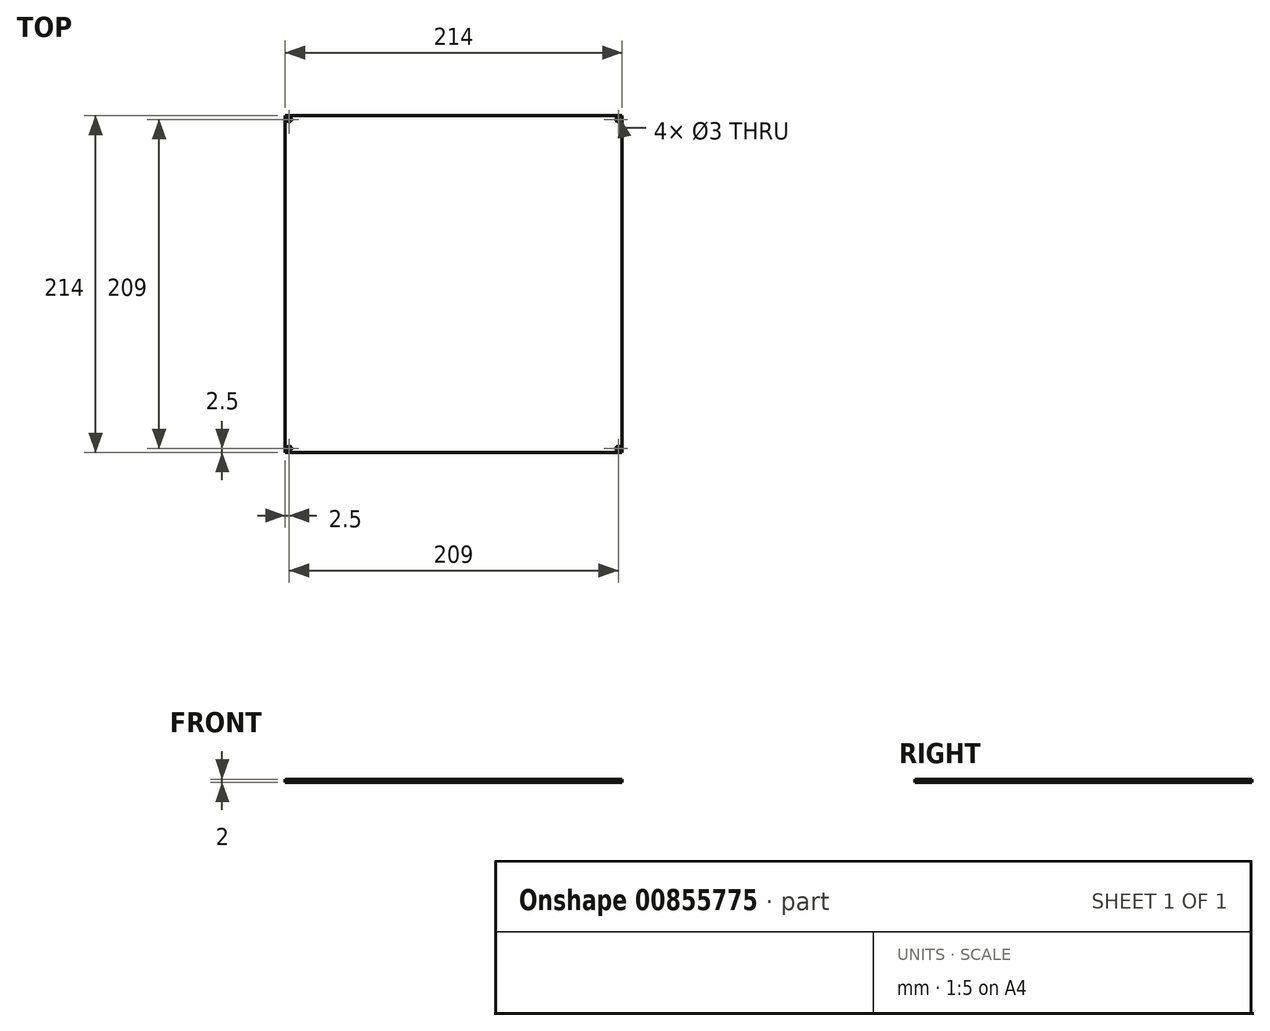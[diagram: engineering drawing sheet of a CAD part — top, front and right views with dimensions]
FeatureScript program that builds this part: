
annotation { "Feature Type Name" : "Feature", "Feature Type Description" : "" }
export const myFeature = defineFeature(function(context is Context, id is Id, definition is map)
    precondition{}
    {
        {
            var Q0;
            Q0=qCreatedBy(makeId("Top.planeOp"),FACE);
            var sketch = newSketch(context, id + "F0", { "sketchPlane" : qUnion([Q0])});
            skLineSegment(sketch, "E0.bottom", {"start": v(-107, 107) * mm, "end": v(107, 107) * mm});
            skLineSegment(sketch, "E0.top", {"start": v(-107, -107) * mm, "end": v(107, -107) * mm});
            skLineSegment(sketch, "E0.left", {"start": v(-107, 107) * mm, "end": v(-107, -107) * mm});
            skLineSegment(sketch, "E0.right", {"start": v(107, 107) * mm, "end": v(107, -107) * mm});
            skPoint(sketch, "E0.middle", {"position": v(0, 0) * mm});
            skLineSegment(sketch, "E1.bottom", {"start": v(-104.5, 104.5) * mm, "end": v(104.5, 104.5) * mm});
            skLineSegment(sketch, "E1.top", {"start": v(-104.5, -104.5) * mm, "end": v(104.5, -104.5) * mm});
            skLineSegment(sketch, "E1.left", {"start": v(-104.5, 104.5) * mm, "end": v(-104.5, -104.5) * mm});
            skLineSegment(sketch, "E1.right", {"start": v(104.5, 104.5) * mm, "end": v(104.5, -104.5) * mm});
            skCircle(sketch, "E2", {"center": v(-104.5, 104.5) * mm, "radius": 1.5 * mm});
            skCircle(sketch, "E3", {"center": v(104.5, 104.5) * mm, "radius": 1.5 * mm});
            skCircle(sketch, "E4", {"center": v(-104.5, -104.5) * mm, "radius": 1.5 * mm});
            skCircle(sketch, "E5", {"center": v(104.5, -104.5) * mm, "radius": 1.5 * mm});
            skSolve(sketch);
        }
        {
            var Q0;
            Q0=makeQuery(id+"F0.imprint","IMPRINT",FACE,{"disambiguationData":[TD([[makeQuery(id+"F0.imprint","IMPRINT",EDGE,{"derivedFrom":sQuery(id+"F0.wireOp",EDGE,"E0.bottom")}),-1.0]])]});
            var Q1;
            {var subQ5=sQuery(id+"F0.wireOp",EDGE,"E2");var subQ13=sQuery(id+"F0.wireOp",EDGE,"E1.bottom");var subQ14=makeQuery(id+"F0.imprint","INTERSECT",VERTEX,{"derivedFrom":[subQ13,subQ5]});Q1=makeQuery(id+"F0.imprint","IMPRINT",FACE,{"disambiguationData":[TD([[makeQuery(id+"F0.imprint","IMPRINT",EDGE,{"disambiguationData":[TD([[subQ14,-1.0]])],"derivedFrom":subQ13}),-1.0]])]});}
            extrude(context, id + "F1", {"entities" : qUnion([Q0, Q1]), "depth" : 2 * mm, "offsetDistance" : 25 * mm});
        }
    });
